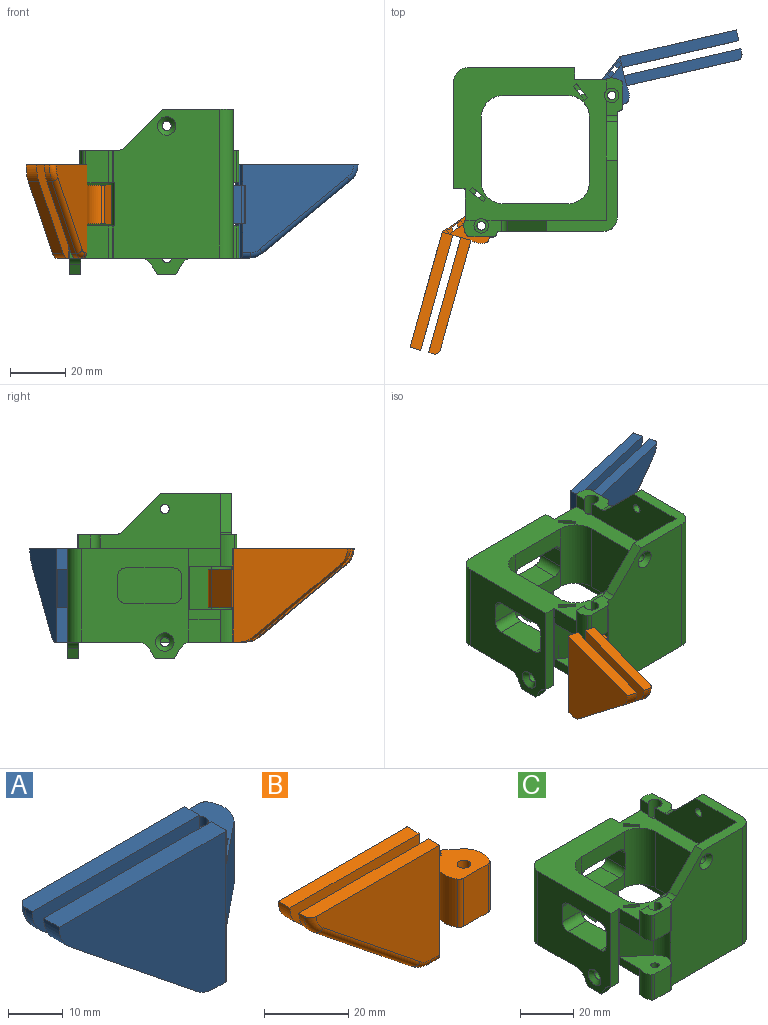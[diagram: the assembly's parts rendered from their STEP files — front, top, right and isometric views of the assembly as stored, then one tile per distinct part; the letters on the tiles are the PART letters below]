
ASSEMBLY  parts=3 mates=2
PART A: 41 faces, bbox 56.2x17x34.4 mm
  f0: plane 2.55x2.5mm, normal (0,0,1), area 3.2mm2, adj f21,f35,f37,f38,f39
  f1: plane 2.56x2.5mm, normal (0,0,1), area 3.2mm2, adj f35,f36,f37,f40
  f2: plane 16.94x12.65mm, normal (0,0,-1), area 133.1mm2, adj f5,f11,f12,f13,f14,f15,f16,f17
  f3: plane 43.28x3.8mm, normal (0,0,1), area 163.6mm2, adj f5,f6,f19,f27,f31
  f4: plane 43.28x4mm, normal (0,0,1), area 173.1mm2, adj f8,f9,f15,f21,f23
  f5: plane 41.35x31.8mm, normal (0,1,0), area 782.2mm2, adj f2,f3,f16,f18,f19,f20,f31,f32
  f6: plane 43.28x33.8mm, normal (0,-1,0), area 891.7mm2, adj f3,f7,f11,f19,f20,f26,f27,f28
  f7: plane 3x1.8mm, normal (0,0,-1), area 5.4mm2, adj f6,f20,f28,f34
  f8: plane 42.93x33.8mm, normal (0,-1,0), area 879.7mm2, adj f4,f10,f15,f23,f24,f25
  f9: plane 43.28x33.8mm, normal (0,1,0), area 891.7mm2, adj f4,f10,f11,f21,f22,f23,f24,f25
  f10: plane 4x3mm, normal (0,0,-1), area 12mm2, adj f8,f9,f15,f22,f25
  f11: plane 14x3mm, normal (-1,0,0), area 42mm2, adj f2,f6,f9,f18
  f12: plane 14x8.25mm, normal (0,1,0), area 115.5mm2, adj f2,f18,f29,f30
  f13: cylinder r=6.32mm len=14mm, axis (0,0,-1), area 127mm2, adj f2,f14,f18,f30
  f14: plane 14x9.71mm, normal (0.63,-0.78,0), area 174.9mm2, adj f2,f13,f15,f18
  f15: cylinder r=1mm len=33.8mm, axis (0,0,-1), area 16.7mm2, adj f2,f4,f8,f10,f14,f18,f21,f22
  f16: cylinder r=6.32mm len=14mm, axis (0,0,-1), area 79.7mm2, adj f2,f5,f18,f29
  f17: cylinder r=1.6mm len=14mm, axis (0,0,-1), area 140.7mm2, adj f2,f18
  f18: plane 16.94x12.65mm, normal (0,0,1), area 126.7mm2, adj f5,f11,f12,f13,f14,f15,f16,f17
  f19: plane 7.4x3.8mm, normal (1,0,0), area 28.1mm2, adj f3,f5,f6,f18
  f20: plane 12.4x3.8mm, normal (1,0,0), area 46.3mm2, adj f2,f5,f6,f7,f34
  f21: plane 20.6x3.94mm, normal (1,0,0), area 29.3mm2, adj f0,f4,f9,f15,f18,f35,f38
  f22: plane 12.4x3.94mm, normal (1,0,0), area 48.8mm2, adj f2,f9,f10,f15
  f23: cylinder r=7.5mm len=6.07mm, axis (0,1,0), area 28.3mm2, adj f4,f8,f9,f24
  f24: plane 32.5x26.08mm, normal (-0.63,0,-0.78), area 166.7mm2, adj f8,f9,f23,f25
  f25: cylinder r=7.5mm len=4.69mm, axis (0,1,0), area 20.3mm2, adj f8,f9,f10,f24
  f26: plane 32.5x26.08mm, normal (-0.63,0,-0.78), area 75mm2, adj f6,f27,f28,f32
  f27: cylinder r=7.5mm len=6.07mm, axis (0,1,0), area 12.7mm2, adj f3,f6,f26,f31
  f28: cylinder r=7.5mm len=4.69mm, axis (0,1,0), area 9.1mm2, adj f6,f7,f26,f33
  f29: cylinder r=1.5mm len=14mm, axis (0,0,-1), area 21.5mm2, adj f2,f12,f16,f18
  f30: cylinder r=1.5mm len=14mm, axis (0,0,-1), area 21.5mm2, adj f2,f12,f13,f18
  f31: torus R=5.5mm, axis (0,1,0), area 20.1mm2, adj f3,f5,f27,f32
  f32: cylinder r=2mm len=33.79mm, axis (0.78,0,-0.63), area 131mm2, adj f5,f26,f31,f33
  f33: torus R=5.5mm, axis (0,1,0), area 14.4mm2, adj f5,f28,f32,f34
  f34: cylinder r=2mm len=3mm, axis (1,0,0), area 9.4mm2, adj f5,f7,f20,f33
  f35: plane 14x4.81mm, normal (0.63,-0.78,0), area 83.5mm2, adj f0,f1,f2,f18,f21,f36,f39,f40
  f36: plane 13.2x1.24mm, normal (-0.78,-0.63,0), area 21.1mm2, adj f1,f18,f35,f37
  f37: plane 14x4.82mm, normal (-0.63,0.78,0), area 83.6mm2, adj f0,f1,f2,f18,f36,f38,f39,f40
  f38: plane 13.2x1.23mm, normal (0.78,0.63,0), area 21mm2, adj f0,f18,f21,f37
  f39: plane 1.24x1.01mm, normal (0.78,0.63,0), area 1.3mm2, adj f0,f2,f35,f37
  f40: plane 1.24x1.01mm, normal (-0.78,-0.63,0), area 1.3mm2, adj f1,f2,f35,f37
PART B: 41 faces, bbox 56.2x17x34.4 mm
  f0: plane 2.55x2.5mm, normal (0,0,1), area 3.2mm2, adj f21,f35,f37,f38,f39
  f1: plane 2.56x2.5mm, normal (0,0,1), area 3.2mm2, adj f35,f36,f37,f40
  f2: plane 16.94x12.65mm, normal (0,0,-1), area 133.1mm2, adj f5,f11,f12,f13,f14,f15,f16,f17
  f3: plane 43.28x3.8mm, normal (0,0,1), area 163.6mm2, adj f5,f6,f19,f27,f31
  f4: plane 43.28x4mm, normal (0,0,1), area 173.1mm2, adj f8,f9,f15,f21,f23
  f5: plane 41.35x31.8mm, normal (0,-1,0), area 782.2mm2, adj f2,f3,f16,f18,f19,f20,f31,f32
  f6: plane 43.28x33.8mm, normal (0,1,0), area 891.7mm2, adj f3,f7,f11,f19,f20,f26,f27,f28
  f7: plane 3x1.8mm, normal (0,0,-1), area 5.4mm2, adj f6,f20,f28,f34
  f8: plane 42.93x33.8mm, normal (0,1,0), area 879.7mm2, adj f4,f10,f15,f23,f24,f25
  f9: plane 43.28x33.8mm, normal (0,-1,0), area 891.7mm2, adj f4,f10,f11,f21,f22,f23,f24,f25
  f10: plane 4x3mm, normal (0,0,-1), area 12mm2, adj f8,f9,f15,f22,f25
  f11: plane 14x3mm, normal (-1,0,0), area 42mm2, adj f2,f6,f9,f18
  f12: plane 14x8.25mm, normal (0,-1,0), area 115.5mm2, adj f2,f18,f29,f30
  f13: cylinder r=6.32mm len=14mm, axis (0,0,-1), area 127mm2, adj f2,f14,f18,f30
  f14: plane 14x9.71mm, normal (0.63,0.78,0), area 174.9mm2, adj f2,f13,f15,f18
  f15: cylinder r=1mm len=33.8mm, axis (0,0,-1), area 16.7mm2, adj f2,f4,f8,f10,f14,f18,f21,f22
  f16: cylinder r=6.32mm len=14mm, axis (0,0,-1), area 79.7mm2, adj f2,f5,f18,f29
  f17: cylinder r=1.6mm len=14mm, axis (0,0,-1), area 140.7mm2, adj f2,f18
  f18: plane 16.94x12.65mm, normal (0,0,1), area 126.7mm2, adj f5,f11,f12,f13,f14,f15,f16,f17
  f19: plane 7.4x3.8mm, normal (1,0,0), area 28.1mm2, adj f3,f5,f6,f18
  f20: plane 12.4x3.8mm, normal (1,0,0), area 46.3mm2, adj f2,f5,f6,f7,f34
  f21: plane 20.6x3.94mm, normal (1,0,0), area 29.3mm2, adj f0,f4,f9,f15,f18,f35,f38
  f22: plane 12.4x3.94mm, normal (1,0,0), area 48.8mm2, adj f2,f9,f10,f15
  f23: cylinder r=7.5mm len=6.07mm, axis (0,-1,0), area 28.3mm2, adj f4,f8,f9,f24
  f24: plane 32.5x26.08mm, normal (-0.63,0,-0.78), area 166.7mm2, adj f8,f9,f23,f25
  f25: cylinder r=7.5mm len=4.69mm, axis (0,-1,0), area 20.3mm2, adj f8,f9,f10,f24
  f26: plane 32.5x26.08mm, normal (-0.63,0,-0.78), area 75mm2, adj f6,f27,f28,f32
  f27: cylinder r=7.5mm len=6.07mm, axis (0,-1,0), area 12.7mm2, adj f3,f6,f26,f31
  f28: cylinder r=7.5mm len=4.69mm, axis (0,-1,0), area 9.1mm2, adj f6,f7,f26,f33
  f29: cylinder r=1.5mm len=14mm, axis (0,0,-1), area 21.5mm2, adj f2,f12,f16,f18
  f30: cylinder r=1.5mm len=14mm, axis (0,0,-1), area 21.5mm2, adj f2,f12,f13,f18
  f31: torus R=5.5mm, axis (0,-1,0), area 20.1mm2, adj f3,f5,f27,f32
  f32: cylinder r=2mm len=33.79mm, axis (0.78,0,-0.63), area 131mm2, adj f5,f26,f31,f33
  f33: torus R=5.5mm, axis (0,-1,0), area 14.4mm2, adj f5,f28,f32,f34
  f34: cylinder r=2mm len=3mm, axis (1,0,0), area 9.4mm2, adj f5,f7,f20,f33
  f35: plane 14x4.81mm, normal (0.63,0.78,0), area 83.5mm2, adj f0,f1,f2,f18,f21,f36,f39,f40
  f36: plane 13.2x1.24mm, normal (-0.78,0.63,0), area 21.1mm2, adj f1,f18,f35,f37
  f37: plane 14x4.82mm, normal (-0.63,-0.78,0), area 83.6mm2, adj f0,f1,f2,f18,f36,f38,f39,f40
  f38: plane 13.2x1.23mm, normal (0.78,-0.63,0), area 21mm2, adj f0,f18,f21,f37
  f39: plane 1.24x1.01mm, normal (0.78,-0.63,0), area 1.3mm2, adj f0,f2,f35,f37
  f40: plane 1.24x1.01mm, normal (-0.78,0.63,0), area 1.3mm2, adj f1,f2,f35,f37
PART C: 138 faces, bbox 61.2x61.2x59.8 mm
  f0: plane 51.2x51.2mm, normal (0,0,-1), area 1125.9mm2, adj f5,f6,f8,f11,f17,f18,f19,f20
  f1: plane 55.2x55.2mm, normal (0,0,1), area 1439.2mm2, adj f5,f7,f8,f12,f13,f17,f18,f19
  f2: plane 17.26x13.05mm, normal (0,0,-1), area 142mm2, adj f22,f23,f32,f33,f38,f39,f40,f41
  f3: plane 17.26x13.05mm, normal (0,0,1), area 142mm2, adj f25,f26,f27,f28,f44,f45,f46,f51
  f4: plane 2.56x2.5mm, normal (0,0,1), area 3.2mm2, adj f119,f120,f122,f124
  f5: cylinder r=8mm len=25.8mm, axis (0,0,-1), area 323.4mm2, adj f0,f1,f6,f11,f12,f21,f101,f114
  f6: plane 23.2x8.23mm, normal (0,-1,0), area 142.6mm2, adj f0,f5,f8,f112,f113,f114
  f7: plane 39.8x38.8mm, normal (0,1,0), area 1047.8mm2, adj f1,f14,f29,f30,f79,f80,f81,f92
  f8: cylinder r=8mm len=25.8mm, axis (0,0,-1), area 323.4mm2, adj f0,f1,f6,f17,f21,f111,f112,f118
  f9: plane 2.56x2.5mm, normal (0,0,1), area 3.2mm2, adj f105,f106,f108,f109
  f10: plane 2.56x2.5mm, normal (0,0,1), area 3.2mm2, adj f106,f107,f108,f110
  f11: plane 23.2x9mm, normal (1,0,0), area 143.1mm2, adj f0,f5,f20,f102,f103,f104
  f12: plane 23.2x10mm, normal (1,0,0), area 166.3mm2, adj f1,f5,f20,f98,f99,f100
  f13: plane 39.8x38.8mm, normal (-1,0,0), area 1051.5mm2, adj f1,f14,f30,f31,f82,f83,f84,f90
  f14: plane 25.39x25.29mm, normal (0,0,-1), area 181.3mm2, adj f7,f13,f30,f63,f64,f93,f95
  f15: plane 13.53x6mm, normal (0,0,1), area 55.4mm2, adj f25,f35,f36,f37,f54,f55,f56,f72
  f16: plane 5.25x5.25mm, normal (0,0,1), area 14.1mm2, adj f42,f54
  f17: plane 25.8x23.2mm, normal (-1,0,0), area 598.6mm2, adj f0,f1,f8,f18
  f18: cylinder r=8mm len=25.8mm, axis (0,0,-1), area 324.2mm2, adj f0,f1,f17,f19
  f19: plane 25.8x23.2mm, normal (0,1,0), area 598.6mm2, adj f0,f1,f18,f20
  f20: cylinder r=8mm len=25.8mm, axis (0,0,-1), area 324.2mm2, adj f0,f1,f11,f12,f19,f97
  f21: plane 23.2x9.23mm, normal (0,-1,0), area 165.8mm2, adj f1,f5,f8,f116,f117,f118
  f22: cylinder r=6.72mm len=15.6mm, axis (0,0,-1), area 125mm2, adj f2,f23,f33,f52
  f23: plane 53.8x38.2mm, normal (0,-1,0), area 1864.1mm2, adj f2,f22,f24,f40,f49,f52,f59,f62
  f24: cylinder r=5mm len=53.8mm, axis (0,0,-1), area 422.5mm2, adj f23,f25,f62,f74
  f25: plane 53.8x38.2mm, normal (1,0,0), area 1864.1mm2, adj f3,f15,f24,f26,f34,f35,f44,f62
  f26: cylinder r=6.72mm len=15.6mm, axis (0,0,-1), area 125mm2, adj f3,f25,f27,f34
  f27: plane 15.6x9.82mm, normal (0.78,0.63,0), area 197.1mm2, adj f3,f26,f28,f34
  f28: cylinder r=1mm len=33.8mm, axis (0,0,-1), area 14.5mm2, adj f1,f3,f27,f29,f34,f63,f96,f132
  f29: plane 33.8x3.79mm, normal (1,0,0), area 128mm2, adj f1,f7,f28,f96
  f30: cylinder r=5mm len=33.8mm, axis (0,0,-1), area 265.5mm2, adj f1,f7,f13,f14
  f31: plane 33.8x3.79mm, normal (0,-1,0), area 128mm2, adj f1,f13,f32,f94
  f32: cylinder r=1mm len=33.8mm, axis (0,0,-1), area 14.5mm2, adj f1,f2,f31,f33,f52,f64,f65,f126
  f33: plane 15.6x9.82mm, normal (-0.63,-0.78,0), area 197.1mm2, adj f2,f22,f32,f52
  f34: plane 17.26x13.05mm, normal (0,0,-1), area 142mm2, adj f25,f26,f27,f28,f35,f36,f37,f42
  f35: cylinder r=6.32mm len=11.6mm, axis (0,0,-1), area 16.4mm2, adj f15,f25,f34,f72
  f36: plane 11.6x8.25mm, normal (1,0,0), area 95.7mm2, adj f15,f34,f72,f73
  f37: cylinder r=6.32mm len=11.6mm, axis (0,0,-1), area 63.6mm2, adj f15,f34,f55,f73
  f38: cylinder r=6.32mm len=11.6mm, axis (0,0,-1), area 63.6mm2, adj f2,f58,f59,f70
  f39: plane 11.6x8.25mm, normal (0,-1,0), area 95.7mm2, adj f2,f59,f70,f71
  f40: cylinder r=6.32mm len=11.6mm, axis (0,0,-1), area 16.4mm2, adj f2,f23,f59,f71
  f41: cylinder r=1.55mm len=3.6mm, axis (0,0,-1), area 35.1mm2, adj f2,f43
  f42: cylinder r=1.55mm len=3.6mm, axis (0,0,-1), area 35.1mm2, adj f16,f34
  f43: plane 5.25x5.25mm, normal (0,0,1), area 14.1mm2, adj f41,f53
  f44: cylinder r=6.32mm len=11.6mm, axis (0,0,1), area 16.4mm2, adj f3,f25,f62,f68
  f45: plane 11.6x8.25mm, normal (1,0,0), area 95.7mm2, adj f3,f62,f68,f69
  f46: cylinder r=6.32mm len=11.6mm, axis (0,0,1), area 63.6mm2, adj f3,f61,f62,f69
  f47: cylinder r=6.32mm len=11.6mm, axis (0,0,1), area 63.6mm2, adj f52,f60,f62,f66
  f48: plane 11.6x8.25mm, normal (0,-1,0), area 95.7mm2, adj f52,f62,f66,f67
  f49: cylinder r=6.32mm len=11.6mm, axis (0,0,1), area 16.4mm2, adj f23,f52,f62,f67
  f50: cylinder r=1.55mm len=11.6mm, axis (0,0,1), area 113mm2, adj f52,f62
  f51: cylinder r=1.55mm len=11.6mm, axis (0,0,1), area 113mm2, adj f3,f62
  f52: plane 17.26x13.05mm, normal (0,0,1), area 142mm2, adj f22,f23,f32,f33,f47,f48,f49,f50
  f53: cylinder r=2.62mm len=8mm, axis (0,0,-1), area 113.5mm2, adj f1,f43,f57,f58,f59
  f54: cylinder r=2.62mm len=8mm, axis (0,0,-1), area 113.5mm2, adj f1,f15,f16,f55,f56
  f55: plane 11.6x4.3mm, normal (-1,0,0), area 23.5mm2, adj f1,f15,f34,f37,f54,f134
  f56: plane 43.5x20mm, normal (-1,0,0), area 647.9mm2, adj f1,f15,f54,f57,f74,f75,f78,f85
  f57: plane 43.5x20mm, normal (0,1,0), area 647.9mm2, adj f1,f53,f56,f59,f74,f76,f77,f87
  f58: plane 11.6x4.3mm, normal (0,1,0), area 23.5mm2, adj f1,f2,f38,f53,f59,f131
  f59: plane 13.53x6mm, normal (0,0,1), area 55.4mm2, adj f23,f38,f39,f40,f53,f57,f58,f70
  f60: plane 51.2x11.6mm, normal (0,1,0), area 410.7mm2, adj f0,f47,f52,f61,f62,f128
  f61: plane 51.2x11.6mm, normal (-1,0,0), area 410.7mm2, adj f0,f3,f46,f60,f62,f137
  f62: plane 57.52x57.52mm, normal (0,0,-1), area 450.7mm2, adj f23,f24,f25,f44,f45,f46,f47,f48
  f63: plane 39.82x14mm, normal (0,-1,0), area 373.6mm2, adj f0,f14,f28,f64,f79,f80,f81,f91
  f64: plane 39.82x14mm, normal (1,0,0), area 374.8mm2, adj f0,f14,f32,f63,f65,f82,f83,f84
  f65: plane 0.21x0.02mm, normal (0,0,-1), area 0mm2, adj f32,f64,f94
  f66: cylinder r=1.5mm len=11.6mm, axis (0,0,1), area 17.9mm2, adj f47,f48,f52,f62
  f67: cylinder r=1.5mm len=11.6mm, axis (0,0,1), area 17.9mm2, adj f48,f49,f52,f62
  f68: cylinder r=1.5mm len=11.6mm, axis (0,0,1), area 17.9mm2, adj f3,f44,f45,f62
  f69: cylinder r=1.5mm len=11.6mm, axis (0,0,1), area 17.9mm2, adj f3,f45,f46,f62
  f70: cylinder r=1.5mm len=11.6mm, axis (0,0,-1), area 17.9mm2, adj f2,f38,f39,f59
  f71: cylinder r=1.5mm len=11.6mm, axis (0,0,-1), area 17.9mm2, adj f2,f39,f40,f59
  f72: cylinder r=1.5mm len=11.6mm, axis (0,0,-1), area 17.9mm2, adj f15,f34,f35,f36
  f73: cylinder r=1.5mm len=11.6mm, axis (0,0,-1), area 17.9mm2, adj f15,f34,f36,f37
  f74: plane 25.75x25.75mm, normal (0,0,1), area 184.6mm2, adj f23,f24,f25,f56,f57,f75,f76
  f75: plane 14.12x14.12mm, normal (0,0.71,0.71), area 79.9mm2, adj f25,f56,f74,f78
  f76: plane 14.12x14.12mm, normal (-0.71,0,0.71), area 79.9mm2, adj f23,f57,f74,f77
  f77: cylinder r=3mm len=4mm, axis (0,1,0), area 9.4mm2, adj f23,f57,f59,f76
  f78: cylinder r=3mm len=4mm, axis (-1,0,0), area 9.4mm2, adj f15,f25,f56,f75
  f79: plane 6.73x4mm, normal (0,0,-1), area 26.9mm2, adj f7,f63,f80,f81
  f80: plane 4x3.5mm, normal (-0.87,0,-0.5), area 16.2mm2, adj f7,f63,f79,f95
  f81: plane 4x3.62mm, normal (0.87,0,-0.5), area 16.7mm2, adj f7,f63,f79,f96
  f82: plane 6.93x4mm, normal (0,0,-1), area 27.7mm2, adj f13,f64,f83,f84
  f83: plane 4x3.5mm, normal (0,0.87,-0.5), area 16.2mm2, adj f13,f64,f82,f93
  f84: plane 4x3.65mm, normal (0,-0.87,-0.5), area 16.8mm2, adj f13,f64,f82,f94
  f85: cylinder r=1.65mm len=3.3mm, axis (1,0,0), area 23.7mm2, adj f56,f86
  f86: cone r=1.65mm half-angle=45deg, axis (1,0,0), area 38.1mm2, adj f25,f85
  f87: cylinder r=1.65mm len=3.3mm, axis (0,-1,0), area 23.7mm2, adj f57,f88
  f88: cone r=1.65mm half-angle=45deg, axis (0,-1,0), area 38.1mm2, adj f23,f87
  f89: cylinder r=1.65mm len=3.3mm, axis (-1,0,0), area 23.7mm2, adj f64,f90
  f90: cone r=1.65mm half-angle=45deg, axis (-1,0,0), area 38.1mm2, adj f13,f89
  f91: cylinder r=1.65mm len=3.3mm, axis (0,1,0), area 23.7mm2, adj f63,f92
  f92: cone r=1.65mm half-angle=45deg, axis (0,1,0), area 38.1mm2, adj f7,f91
  f93: cylinder r=5mm len=4.33mm, axis (-1,0,0), area 20.9mm2, adj f13,f14,f64,f83
  f94: cylinder r=5mm len=4mm, axis (1,0,0), area 16.1mm2, adj f13,f31,f64,f65,f84
  f95: cylinder r=5mm len=4.33mm, axis (0,-1,0), area 20.9mm2, adj f7,f14,f63,f80
  f96: cylinder r=5mm len=4mm, axis (0,-1,0), area 16.6mm2, adj f7,f28,f29,f63,f81
  f97: plane 10x6.8mm, normal (0,1,0), area 68mm2, adj f13,f20,f98,f104
  f98: cylinder r=3mm len=10mm, axis (-1,0,0), area 47.1mm2, adj f12,f13,f97,f99
  f99: plane 17.2x10mm, normal (0,0,-1), area 172mm2, adj f12,f13,f98,f100
  f100: cylinder r=3mm len=10mm, axis (-1,0,0), area 47.1mm2, adj f12,f13,f99,f101
  f101: plane 10x6.8mm, normal (0,-1,0), area 68mm2, adj f5,f13,f100,f102
  f102: cylinder r=3mm len=10mm, axis (-1,0,0), area 47.1mm2, adj f11,f13,f101,f103
  f103: plane 17.2x10mm, normal (0,0,1), area 172mm2, adj f11,f13,f102,f104
  f104: cylinder r=3mm len=10mm, axis (-1,0,0), area 47.1mm2, adj f11,f13,f97,f103
  f105: plane 22x1.24mm, normal (-0.78,0.63,0), area 35.2mm2, adj f1,f9,f106,f108
  f106: plane 25.8x4.82mm, normal (-0.63,-0.78,0), area 144.8mm2, adj f0,f1,f9,f10,f105,f107,f109,f110
  f107: plane 22x1.24mm, normal (0.78,-0.63,0), area 35.2mm2, adj f1,f10,f106,f108
  f108: plane 25.8x4.82mm, normal (0.63,0.78,0), area 144.8mm2, adj f0,f1,f9,f10,f105,f107,f109,f110
  f109: plane 3.8x1.24mm, normal (-0.78,0.63,0), area 6.1mm2, adj f0,f9,f106,f108
  f110: plane 3.8x1.24mm, normal (0.78,-0.63,0), area 6.1mm2, adj f0,f10,f106,f108
  f111: plane 10x6.8mm, normal (-1,0,0), area 68mm2, adj f7,f8,f112,f118
  f112: cylinder r=3mm len=10mm, axis (0,1,0), area 47.1mm2, adj f6,f7,f8,f111,f113
  f113: plane 17.4x10mm, normal (0,0,1), area 174mm2, adj f6,f7,f112,f114
  f114: cylinder r=3mm len=10mm, axis (0,1,0), area 47.1mm2, adj f5,f6,f7,f113,f115
  f115: plane 10x6.8mm, normal (1,0,0), area 68mm2, adj f5,f7,f114,f116
  f116: cylinder r=3mm len=10mm, axis (0,1,0), area 47.1mm2, adj f5,f7,f21,f115,f117
  f117: plane 17.4x10mm, normal (0,0,-1), area 174mm2, adj f7,f21,f116,f118
  f118: cylinder r=3mm len=10mm, axis (0,1,0), area 47.1mm2, adj f7,f8,f21,f111,f117
  f119: plane 22x1.24mm, normal (-0.63,0.78,0), area 35.2mm2, adj f1,f4,f120,f122
  f120: plane 25.8x4.82mm, normal (-0.78,-0.63,0), area 144.8mm2, adj f0,f1,f4,f119,f121,f123,f124,f125
  f121: plane 22x1.24mm, normal (0.63,-0.78,0), area 35.2mm2, adj f1,f120,f122,f123
  f122: plane 25.8x4.82mm, normal (0.78,0.63,0), area 144.8mm2, adj f0,f1,f4,f119,f121,f123,f124,f125
  f123: plane 2.56x2.5mm, normal (0,0,1), area 3.2mm2, adj f120,f121,f122,f125
  f124: plane 3.8x1.24mm, normal (-0.63,0.78,0), area 6.1mm2, adj f0,f4,f120,f122
  f125: plane 3.8x1.24mm, normal (0.63,-0.78,0), area 6.1mm2, adj f0,f120,f122,f123
  f126: plane 0.3x0.12mm, normal (0,0,-1), area 0mm2, adj f32,f127,f128
  f127: plane 3.6x0.3mm, normal (0,-1,0), area 1.1mm2, adj f0,f32,f126,f128
  f128: plane 11.38x3.6mm, normal (-1,0,0), area 41mm2, adj f0,f52,f60,f126,f127
  f129: plane 6.6x0.3mm, normal (0,-1,0), area 2mm2, adj f1,f32,f130,f131
  f130: plane 0.3x0.12mm, normal (0,0,1), area 0mm2, adj f32,f129,f131
  f131: plane 11.38x6.6mm, normal (-1,0,0), area 75.1mm2, adj f1,f2,f58,f129,f130
  f132: plane 0.3x0.12mm, normal (0,0,1), area 0mm2, adj f28,f133,f134
  f133: plane 6.6x0.3mm, normal (1,0,0), area 2mm2, adj f1,f28,f132,f134
  f134: plane 11.38x6.6mm, normal (0,1,0), area 75.1mm2, adj f1,f34,f55,f132,f133
  f135: plane 0.3x0.12mm, normal (0,0,-1), area 0mm2, adj f28,f136,f137
  f136: plane 3.6x0.3mm, normal (1,0,0), area 1.1mm2, adj f0,f28,f135,f137
  f137: plane 11.38x3.6mm, normal (0,1,0), area 41mm2, adj f0,f3,f61,f135,f136
PLACE A rot(axis=(0,0,-1),167.1deg) t=(-8.74,-55.73,28.34)mm
PLACE B rot(axis=(0,0,1),74.4deg) t=(-81.46,-1.6,28.34)mm
PLACE C t=(-36.32,1.1,28.34)mm fixed
MATE revolute C.f22 <-> B.f13  axis (0,0,1) through (-55.92,-26.5,20.54)mm
MATE revolute A.f13 <-> C.f26  axis (0,0,-1) through (-8.72,20.7,28.34)mm
